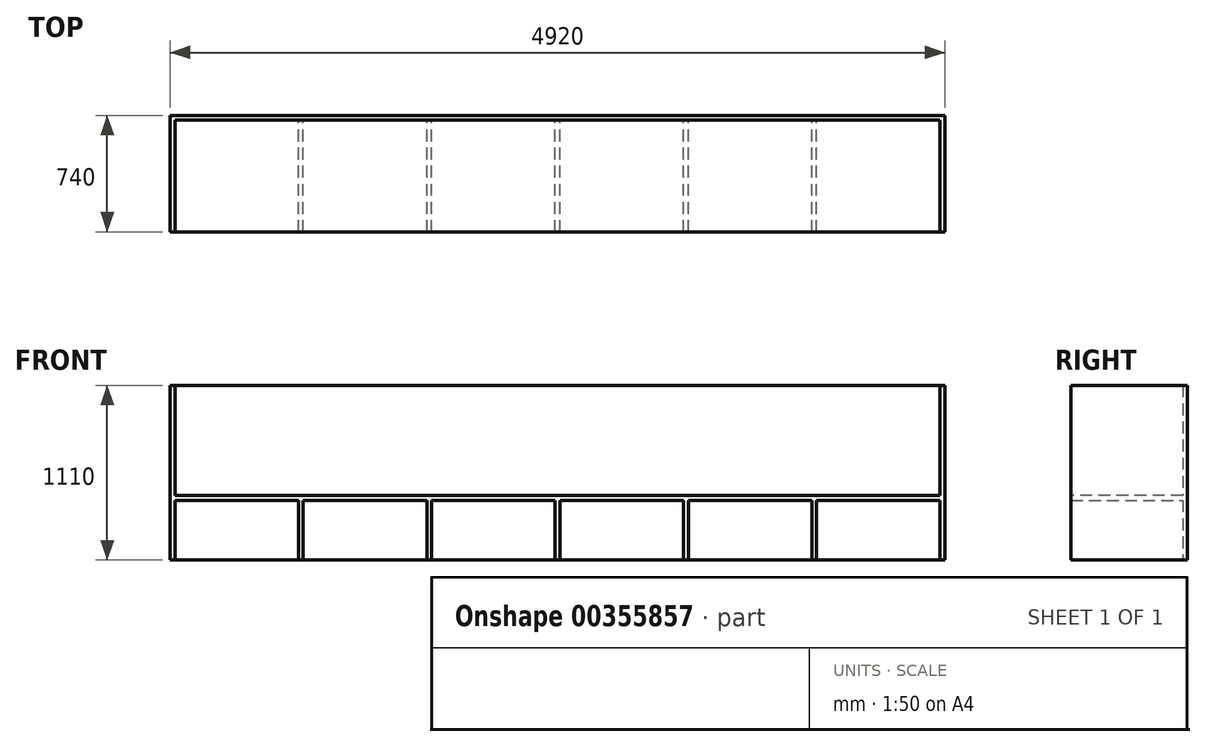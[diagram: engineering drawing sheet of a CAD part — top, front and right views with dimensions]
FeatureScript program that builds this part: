
annotation { "Feature Type Name" : "Feature", "Feature Type Description" : "" }
export const myFeature = defineFeature(function(context is Context, id is Id, definition is map)
    precondition{}
    {
        {
            var Q0;
            Q0=qCreatedBy(makeId("Front.planeOp"),FACE);
            var sketch = newSketch(context, id + "F0", { "sketchPlane" : qUnion([Q0])});
            skLineSegment(sketch, "E0.bottom", {"start": v(-505.56, 240.93) * mm, "end": v(4414.44, 240.93) * mm});
            skLineSegment(sketch, "E0.top", {"start": v(-475.56, 210.93) * mm, "end": v(309.44, 210.93) * mm});
            skLineSegment(sketch, "E0.left", {"start": v(-505.56, 240.93) * mm, "end": v(-505.56, 210.93) * mm});
            skLineSegment(sketch, "E0.right", {"start": v(4414.44, 240.93) * mm, "end": v(4414.44, 210.93) * mm});
            skLineSegment(sketch, "E1.top", {"start": v(-505.56, -169.07) * mm, "end": v(-475.56, -169.07) * mm});
            skLineSegment(sketch, "E1.left", {"start": v(-505.56, 210.93) * mm, "end": v(-505.56, -169.07) * mm});
            skLineSegment(sketch, "E1.right", {"start": v(-475.56, 210.93) * mm, "end": v(-475.56, -169.07) * mm});
            skLineSegment(sketch, "E2.top", {"start": v(4414.44, -169.07) * mm, "end": v(4384.44, -169.07) * mm});
            skLineSegment(sketch, "E2.left", {"start": v(4414.44, 210.93) * mm, "end": v(4414.44, -169.07) * mm});
            skLineSegment(sketch, "E2.right", {"start": v(4384.44, 210.93) * mm, "end": v(4384.44, -169.07) * mm});
            skLineSegment(sketch, "E3", {"start": v(2754.44, -169.07) * mm, "end": v(2784.44, -169.07) * mm});
            skLineSegment(sketch, "E4", {"start": v(1124.44, -169.07) * mm, "end": v(1124.44, 210.93) * mm});
            skLineSegment(sketch, "E5", {"start": v(1154.44, 210.93) * mm, "end": v(1154.44, -169.07) * mm});
            skPoint(sketch, "E6.end.orphan", {"position": v(1154.44, -45.9) * mm});
            skLineSegment(sketch, "E7.left", {"start": v(2754.44, -169.07) * mm, "end": v(2754.44, 210.93) * mm});
            skLineSegment(sketch, "E7.right", {"start": v(2784.44, -169.07) * mm, "end": v(2784.44, 210.93) * mm});
            skLineSegment(sketch, "E8.trimOffspring", {"start": v(4384.44, -169.07) * mm, "end": v(4414.44, -169.07) * mm});
            skLineSegment(sketch, "E9.trimOffspring", {"start": v(2784.44, 210.93) * mm, "end": v(3569.44, 210.93) * mm});
            skLineSegment(sketch, "E10", {"start": v(1124.44, -169.07) * mm, "end": v(1154.44, -169.07) * mm});
            skLineSegment(sketch, "E11.trimOffspring", {"start": v(1154.44, 210.93) * mm, "end": v(1939.44, 210.93) * mm});
            skLineSegment(sketch, "E12", {"start": v(3584.44, -169.07) * mm, "end": v(3569.44, -169.07) * mm});
            skLineSegment(sketch, "E13", {"start": v(3569.44, -169.07) * mm, "end": v(3569.44, 210.93) * mm});
            skLineSegment(sketch, "E14.MirrorCS", {"start": v(3599.44, -169.07) * mm, "end": v(3599.44, 210.93) * mm});
            skLineSegment(sketch, "E15.MirrorCS", {"start": v(3584.44, -169.07) * mm, "end": v(3599.44, -169.07) * mm});
            skPoint(sketch, "E16.start.orphan", {"position": v(3584.44, 210.93) * mm});
            skLineSegment(sketch, "E17.trimOffspring", {"start": v(3599.44, 210.93) * mm, "end": v(4384.44, 210.93) * mm});
            skLineSegment(sketch, "E18", {"start": v(1954.44, -169.07) * mm, "end": v(1939.44, -169.07) * mm});
            skLineSegment(sketch, "E19", {"start": v(1939.44, -169.07) * mm, "end": v(1939.44, 210.93) * mm});
            skLineSegment(sketch, "E20.MirrorCS", {"start": v(1954.44, -169.07) * mm, "end": v(1969.44, -169.07) * mm});
            skLineSegment(sketch, "E21.MirrorCS", {"start": v(1969.44, -169.07) * mm, "end": v(1969.44, 210.93) * mm});
            skLineSegment(sketch, "E22.trimOffspring", {"start": v(1969.44, 210.93) * mm, "end": v(2754.44, 210.93) * mm});
            skPoint(sketch, "E23.start.orphan", {"position": v(1954.44, 210.93) * mm});
            skLineSegment(sketch, "E24", {"start": v(324.44, -169.07) * mm, "end": v(309.44, -169.07) * mm});
            skLineSegment(sketch, "E25", {"start": v(309.44, -169.07) * mm, "end": v(309.44, 210.93) * mm});
            skLineSegment(sketch, "E26.MirrorCS", {"start": v(339.44, -169.07) * mm, "end": v(339.44, 210.93) * mm});
            skLineSegment(sketch, "E27.MirrorCS", {"start": v(324.44, -169.07) * mm, "end": v(339.44, -169.07) * mm});
            skPoint(sketch, "E28.start.orphan", {"position": v(324.44, 210.93) * mm});
            skLineSegment(sketch, "E29.trimOffspring", {"start": v(339.44, 210.93) * mm, "end": v(1124.44, 210.93) * mm});
            skSolve(sketch);
        }
        {
            var Q0;
            Q0 = qSketchRegion(id + "F0", true);
            extrude(context, id + "F1", {"entities" : qUnion([Q0]), "depth" : 740 * mm});
        }
        {
            var Q0;
            Q0=makeQuery(id+"F1.opExtrude","SWEPT_FACE",FACE,{"disambiguationData":[OSD([sQuery(id+"F0.wireOp",EDGE,"E0.bottom")])]});
            var sketch = newSketch(context, id + "F2", { "sketchPlane" : qUnion([Q0])});
            skLineSegment(sketch, "E30.bottom", {"start": v(-505.56, 0) * mm, "end": v(4414.44, 0) * mm});
            skLineSegment(sketch, "E30.top", {"start": v(-505.56, -30) * mm, "end": v(4414.44, -30) * mm});
            skLineSegment(sketch, "E30.left", {"start": v(-505.56, 0) * mm, "end": v(-505.56, -30) * mm});
            skLineSegment(sketch, "E30.right", {"start": v(4414.44, 0) * mm, "end": v(4414.44, -30) * mm});
            skLineSegment(sketch, "E31.bottom", {"start": v(-505.56, 0) * mm, "end": v(-475.56, 0) * mm});
            skLineSegment(sketch, "E31.top", {"start": v(-505.56, -740) * mm, "end": v(-475.56, -740) * mm});
            skLineSegment(sketch, "E31.left", {"start": v(-505.56, 0) * mm, "end": v(-505.56, -740) * mm});
            skLineSegment(sketch, "E31.right", {"start": v(-475.56, 0) * mm, "end": v(-475.56, -740) * mm});
            skLineSegment(sketch, "E32.bottom", {"start": v(4414.44, 0) * mm, "end": v(4384.44, 0) * mm});
            skLineSegment(sketch, "E32.top", {"start": v(4414.44, -740) * mm, "end": v(4384.44, -740) * mm});
            skLineSegment(sketch, "E32.left", {"start": v(4414.44, 0) * mm, "end": v(4414.44, -740) * mm});
            skLineSegment(sketch, "E32.right", {"start": v(4384.44, 0) * mm, "end": v(4384.44, -740) * mm});
            skSolve(sketch);
        }
        {
            var Q0;
            Q0 = qSketchRegion(id + "F2", true);
            extrude(context, id + "F3", {"entities" : qUnion([Q0]), "operationType" : NewBodyOperationType.ADD, "depth" : 700 * mm});
        }
        {
            var Q0;
            Q0=makeQuery(id+"F1.opExtrude","SWEPT_FACE",FACE,{"disambiguationData":[OSD([sQuery(id+"F0.wireOp",EDGE,"E17.trimOffspring")])]});
            var sketch = newSketch(context, id + "F4", { "sketchPlane" : qUnion([Q0])});
            skLineSegment(sketch, "E33.0", {"start": v(4414.44, 30) * mm, "end": v(4414.44, 0) * mm});
            skLineSegment(sketch, "E34.0", {"start": v(-505.56, 30) * mm, "end": v(-505.56, 0) * mm});
            skLineSegment(sketch, "E35", {"start": v(-505.56, 0) * mm, "end": v(4414.44, 0) * mm});
            skLineSegment(sketch, "E36", {"start": v(3053.95, 0) * mm, "end": v(3053.95, 30) * mm});
            skLineSegment(sketch, "E37", {"start": v(4414.44, 30) * mm, "end": v(-505.56, 30) * mm});
            skPoint(sketch, "E38.orphan", {"position": v(-505.56, 740) * mm});
            skPoint(sketch, "E39.orphan", {"position": v(4414.44, 740) * mm});
            skSolve(sketch);
        }
        {
            var Q0;
            Q0 = qSketchRegion(id + "F4", true);
            var Q1;
            Q1=makeQuery(id+"F1.opExtrude","SWEPT_FACE",FACE,{"disambiguationData":[OSD([sQuery(id+"F0.wireOp",EDGE,"E10")])]});
            extrude(context, id + "F5", {"entities" : qUnion([Q0]), "operationType" : NewBodyOperationType.ADD, "endBound" : BoundingType.UP_TO_SURFACE, "endBoundEntityFace" : qUnion([Q1]), "depth" : 25 * mm});
        }
    });
